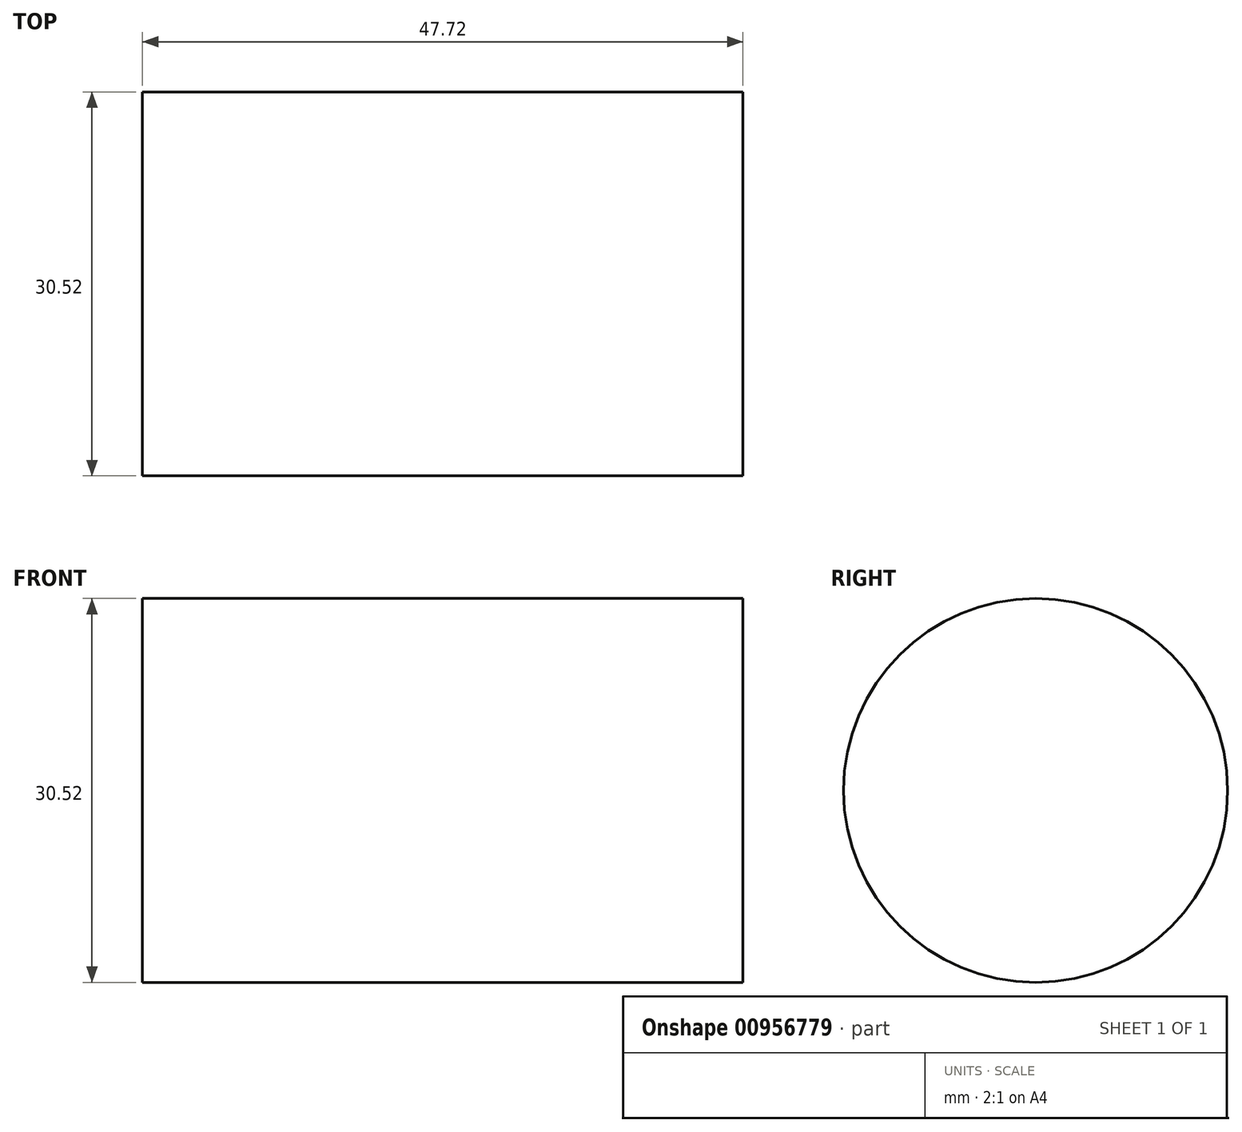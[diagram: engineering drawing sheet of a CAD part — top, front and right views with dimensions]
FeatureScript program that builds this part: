
annotation { "Feature Type Name" : "Feature", "Feature Type Description" : "" }
export const myFeature = defineFeature(function(context is Context, id is Id, definition is map)
    precondition{}
    {
        {
            var Q0;
            Q0=qCreatedBy(makeId("Front.planeOp"),FACE);
            var sketch = newSketch(context, id + "F0", { "sketchPlane" : qUnion([Q0])});
            skLineSegment(sketch, "E0", {"start": v(0, 0) * mm, "end": v(0, 15.26) * mm});
            skLineSegment(sketch, "E1", {"start": v(0, 15.26) * mm, "end": v(47.72, 15.26) * mm});
            skLineSegment(sketch, "E2", {"start": v(47.72, 15.26) * mm, "end": v(47.72, 0) * mm});
            skLineSegment(sketch, "E3", {"start": v(0, 0) * mm, "end": v(47.72, 0) * mm});
            skSolve(sketch);
        }
        {
            var Q0;
            Q0=makeQuery(id+"F0.imprint","IMPRINT",FACE,{"disambiguationData":[TD([[makeQuery(id+"F0.imprint","IMPRINT",EDGE,{"derivedFrom":sQuery(id+"F0.wireOp",EDGE,"E0")}),-1.0]])]});
            var Q1;
            Q1=sQuery(id+"F0.wireOp",EDGE,"E3");
            revolve(context, id + "F1", {"surfaceOperationType" : NewSurfaceOperationType.NEW, "entities" : qUnion([Q0]), "axis" : qUnion([Q1]), "revolveType" : RevolveType.FULL});
        }
    });
